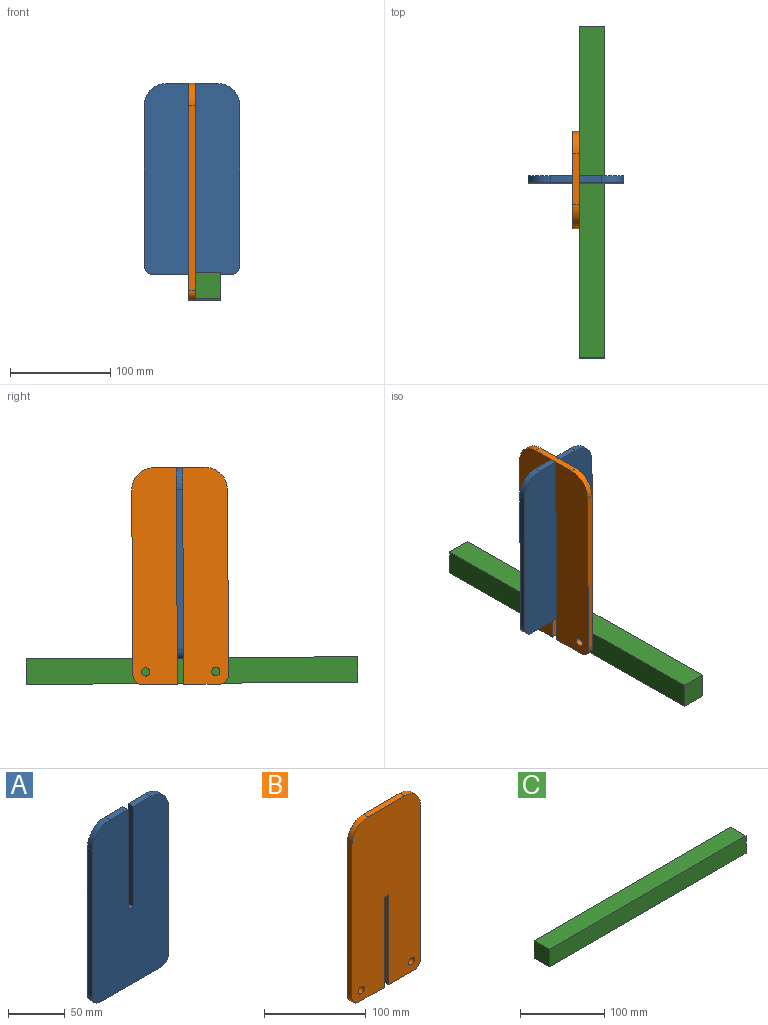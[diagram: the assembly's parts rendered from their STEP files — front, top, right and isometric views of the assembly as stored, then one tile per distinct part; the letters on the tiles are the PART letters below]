
ASSEMBLY  parts=3 mates=2
PART A: 14 faces, bbox 95.3x6.4x190.5 mm
  f0: cylinder r=9.53mm len=9.53mm, axis (0,1,0), area 95mm2, adj f1,f11,f12,f13
  f1: plane 158.75x6.35mm, normal (1,0,0), area 1008.1mm2, adj f0,f2,f12,f13
  f2: cylinder r=22.23mm len=22.23mm, axis (0,1,0), area 221.7mm2, adj f1,f3,f12,f13
  f3: plane 22.23x6.35mm, normal (0,0,1), area 141.1mm2, adj f2,f4,f12,f13
  f4: plane 107.95x6.35mm, normal (-1,0,0), area 685.5mm2, adj f3,f5,f12,f13
  f5: plane 6.35x6.35mm, normal (0,0,1), area 40.3mm2, adj f4,f6,f12,f13
  f6: plane 107.95x6.35mm, normal (1,0,0), area 685.5mm2, adj f5,f7,f12,f13
  f7: plane 22.23x6.35mm, normal (0,0,1), area 141.1mm2, adj f6,f8,f12,f13
  f8: cylinder r=22.23mm len=22.23mm, axis (0,1,0), area 221.7mm2, adj f7,f9,f12,f13
  f9: plane 158.75x6.35mm, normal (-1,0,0), area 1008.1mm2, adj f8,f10,f12,f13
  f10: cylinder r=9.53mm len=9.53mm, axis (0,1,0), area 95mm2, adj f9,f11,f12,f13
  f11: plane 76.2x6.35mm, normal (0,0,-1), area 483.9mm2, adj f0,f10,f12,f13
  f12: plane 190.5x95.25mm, normal (0,-1,0), area 17208.7mm2, adj f0,f1,f2,f3,f4,f5,f6,f7
  f13: plane 190.5x95.25mm, normal (0,1,0), area 17208.7mm2, adj f0,f1,f2,f3,f4,f5,f6,f7
PART B: 16 faces, bbox 95.3x6.4x215.9 mm
  f0: cylinder r=22.23mm len=22.23mm, axis (0,1,0), area 221.7mm2, adj f1,f13,f14,f15
  f1: plane 50.8x6.35mm, normal (0,0,1), area 322.6mm2, adj f0,f2,f14,f15
  f2: cylinder r=22.23mm len=22.23mm, axis (0,1,0), area 221.7mm2, adj f1,f3,f14,f15
  f3: plane 184.15x6.35mm, normal (-1,0,0), area 1169.4mm2, adj f2,f4,f14,f15
  f4: cylinder r=9.53mm len=9.53mm, axis (0,1,0), area 95mm2, adj f3,f5,f14,f15
  f5: plane 35.18x6.35mm, normal (0,0,-1), area 223.4mm2, adj f4,f6,f14,f15
  f6: plane 107.95x6.35mm, normal (1,0,0), area 685.5mm2, adj f5,f7,f14,f15
  f7: plane 6.35x6.1mm, normal (0,0,-1), area 38.7mm2, adj f6,f8,f14,f15
  f8: plane 107.95x6.35mm, normal (-1,0,0), area 685.5mm2, adj f7,f9,f14,f15
  f9: plane 34.93x6.35mm, normal (0,0,-1), area 221.8mm2, adj f8,f10,f14,f15
  f10: cylinder r=9.53mm len=9.53mm, axis (0,1,0), area 95mm2, adj f9,f13,f14,f15
  f11: cylinder r=4.13mm len=8.26mm, axis (0,1,0), area 164.7mm2, adj f14,f15
  f12: cylinder r=4.13mm len=8.26mm, axis (0,1,0), area 164.7mm2, adj f14,f15
  f13: plane 184.15x6.35mm, normal (1,0,0), area 1169.4mm2, adj f0,f10,f14,f15
  f14: plane 215.9x95.25mm, normal (0,-1,0), area 19548.4mm2, adj f0,f1,f2,f3,f4,f5,f6,f7
  f15: plane 215.9x95.25mm, normal (0,1,0), area 19548.4mm2, adj f0,f1,f2,f3,f4,f5,f6,f7
PART C: 6 faces, bbox 330.2x25.4x25.4 mm
  f0: plane 330.2x25.4mm, normal (0,0,1), area 8387.1mm2, adj f1,f3,f4,f5
  f1: plane 25.4x25.4mm, normal (-1,0,0), area 645.2mm2, adj f0,f2,f4,f5
  f2: plane 330.2x25.4mm, normal (0,0,-1), area 8387.1mm2, adj f1,f3,f4,f5
  f3: plane 25.4x25.4mm, normal (1,0,0), area 645.2mm2, adj f0,f2,f4,f5
  f4: plane 330.2x25.4mm, normal (0,-1,0), area 8387.1mm2, adj f0,f1,f2,f3
  f5: plane 330.2x25.4mm, normal (0,1,0), area 8387.1mm2, adj f0,f1,f2,f3
PLACE A rot(axis=(-1,0,0),0.4deg) t=(146.81,167.58,-22.98)mm
PLACE B rot(axis=(0,0,1),90deg) t=(143.64,164.19,-35.66)mm
PLACE C rot(axis=(0,0,-1),90deg) t=(175.39,438.8,-173.32)mm
MATE planar B.f14 <-> C.f4  axis (1,0,0) through (149.99,164.19,-34.23)mm
MATE fastened B.f7 <-> A.f5  axis (0,-0.01,-1) through (146.81,164.32,-35.66)mm
